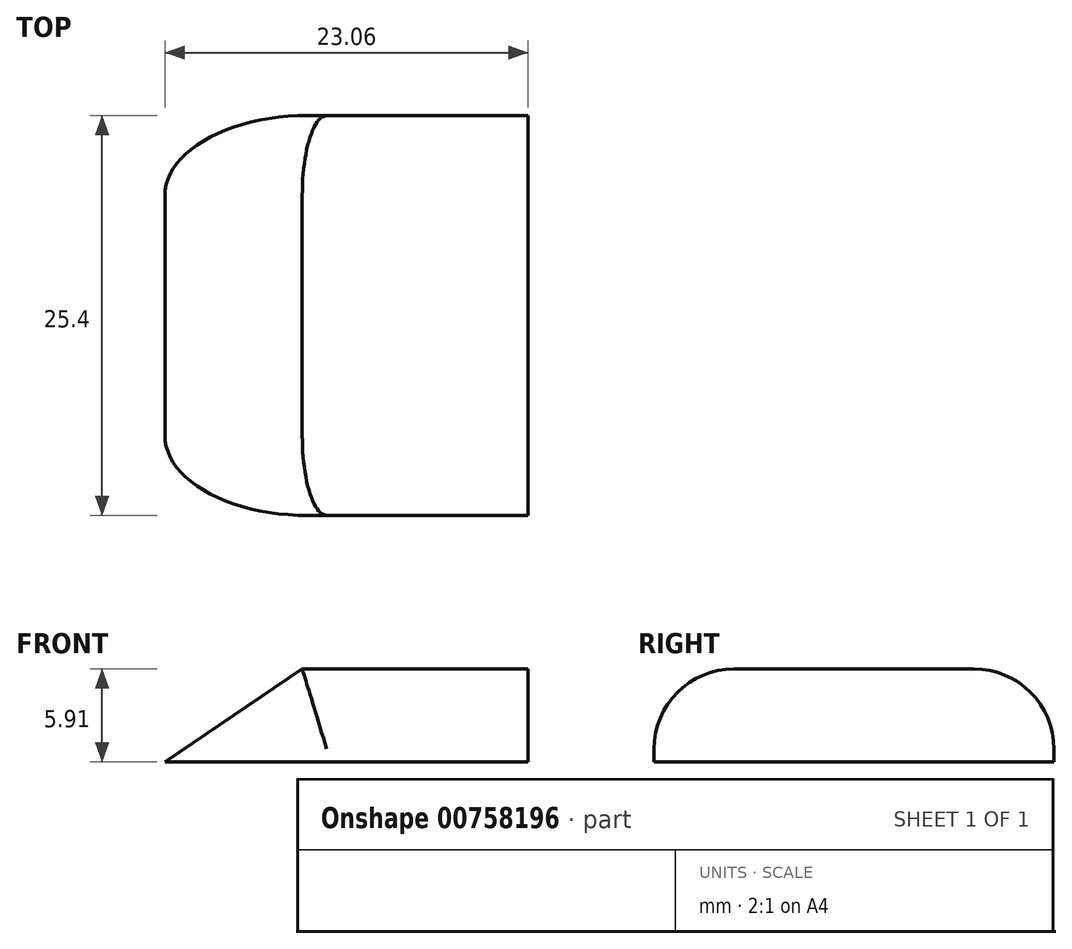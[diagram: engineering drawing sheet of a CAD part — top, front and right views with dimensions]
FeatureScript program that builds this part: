
annotation { "Feature Type Name" : "Feature", "Feature Type Description" : "" }
export const myFeature = defineFeature(function(context is Context, id is Id, definition is map)
    precondition{}
    {
        {
            var Q0;
            Q0=qCreatedBy(makeId("Front.planeOp"),FACE);
            var sketch = newSketch(context, id + "F0", { "sketchPlane" : qUnion([Q0])});
            skLineSegment(sketch, "E0", {"start": v(-53.3, 0) * mm, "end": v(-44.57, 5.9) * mm});
            skLineSegment(sketch, "E1", {"start": v(-44.57, 5.9) * mm, "end": v(-30.23, 5.9) * mm});
            skLineSegment(sketch, "E2", {"start": v(-30.23, 5.9) * mm, "end": v(-30.23, 0) * mm});
            skLineSegment(sketch, "E3", {"start": v(-30.23, 0) * mm, "end": v(-53.3, 0) * mm});
            skSolve(sketch);
        }
        {
            var Q0;
            Q0=makeQuery(id+"F0.imprint","IMPRINT",FACE,{"disambiguationData":[TD([[makeQuery(id+"F0.imprint","IMPRINT",EDGE,{"derivedFrom":sQuery(id+"F0.wireOp",EDGE,"E0")}),-1.0]])]});
            extrude(context, id + "F1", {"entities" : qUnion([Q0]), "depth" : 25.4 * mm, "offsetDistance" : 25.4 * mm});
        }
        {
            var Q0;
            Q0=makeQuery(id+"F1.opExtrude","CAP_EDGE",EDGE,{"disambiguationData":[OSD([sQuery(id+"F0.wireOp",EDGE,"E1")])],"isStart":false});
            var Q1;
            Q1=makeQuery(id+"F1.opExtrude","CAP_EDGE",EDGE,{"disambiguationData":[OSD([sQuery(id+"F0.wireOp",EDGE,"E0")])],"isStart":false});
            var Q2;
            Q2=makeQuery(id+"F1.opExtrude","CAP_EDGE",EDGE,{"disambiguationData":[OSD([sQuery(id+"F0.wireOp",EDGE,"E1")])],"isStart":true});
            var Q3;
            Q3=makeQuery(id+"F1.opExtrude","CAP_EDGE",EDGE,{"disambiguationData":[OSD([sQuery(id+"F0.wireOp",EDGE,"E0")])],"isStart":true});
            fillet(context, id + "F2", {"entities" : qUnion([Q0, Q1, Q2, Q3]), "radius" : 5.08 * mm, "tangentPropagation" : true, "allowEdgeOverflow" : false});
        }
    });
